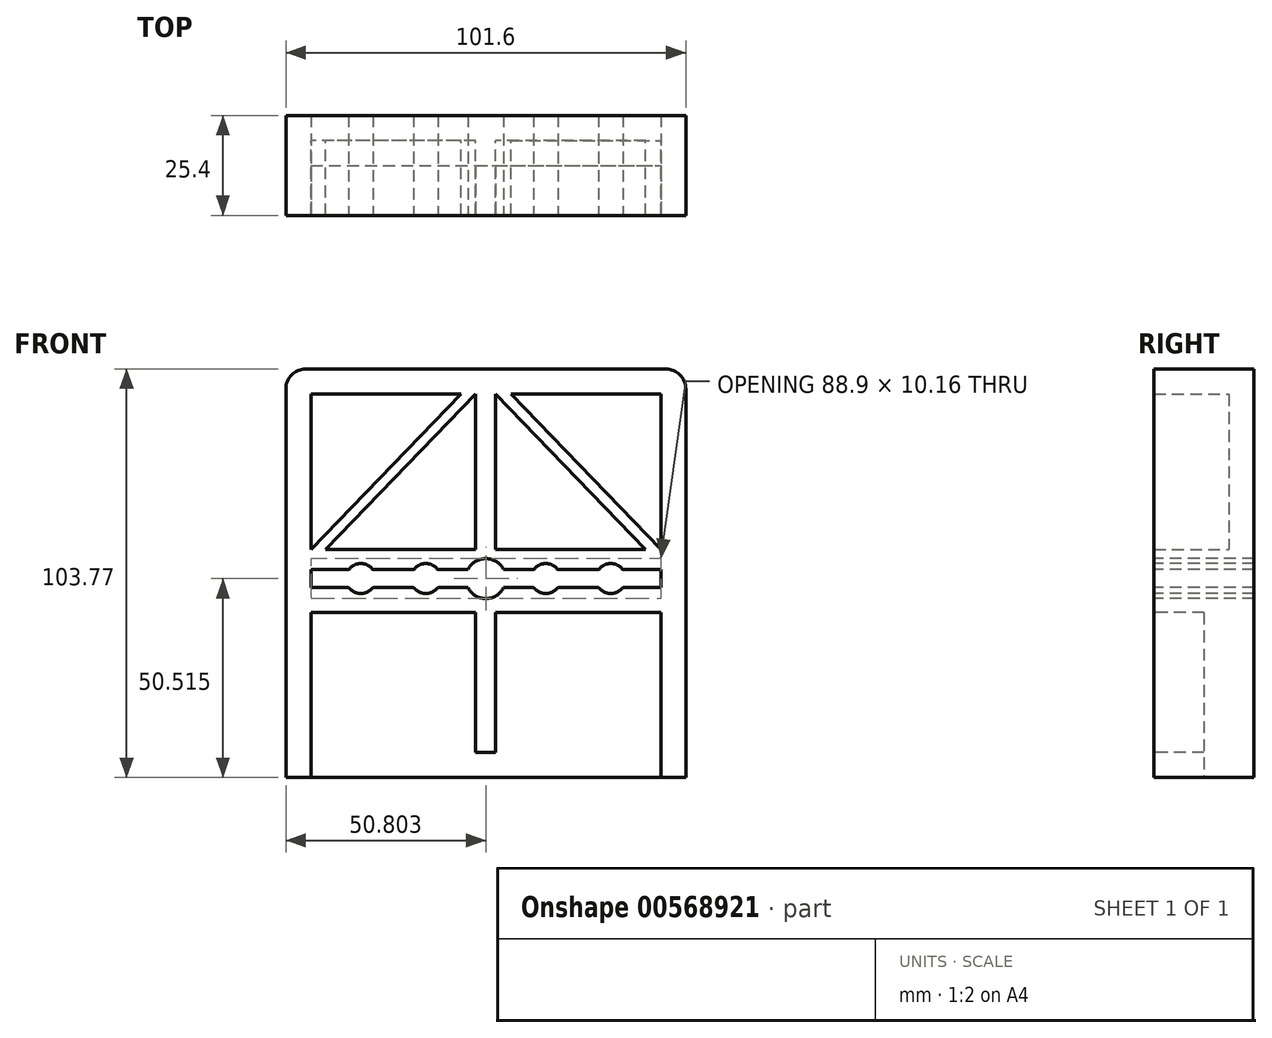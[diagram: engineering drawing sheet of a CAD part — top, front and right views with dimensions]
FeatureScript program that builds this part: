
annotation { "Feature Type Name" : "Feature", "Feature Type Description" : "" }
export const myFeature = defineFeature(function(context is Context, id is Id, definition is map)
    precondition{}
    {
        {
            var Q0;
            Q0=qCreatedBy(makeId("Front.planeOp"),FACE);
            var sketch = newSketch(context, id + "F0", { "sketchPlane" : qUnion([Q0])});
            skLineSegment(sketch, "E0.bottom", {"start": v(-51.37, 49.18) * mm, "end": v(50.23, 49.18) * mm});
            skLineSegment(sketch, "E0.top", {"start": v(-51.37, -54.59) * mm, "end": v(50.23, -54.59) * mm});
            skLineSegment(sketch, "E0.left", {"start": v(-51.37, 49.18) * mm, "end": v(-51.37, -54.59) * mm});
            skLineSegment(sketch, "E0.right", {"start": v(50.23, 49.18) * mm, "end": v(50.23, -54.59) * mm});
            skLineSegment(sketch, "E1", {"start": v(-45.02, 42.83) * mm, "end": v(-45.02, 3.28) * mm});
            skLineSegment(sketch, "E2", {"start": v(-45.02, 3.28) * mm, "end": v(-6.92, 42.83) * mm});
            skLineSegment(sketch, "E3", {"start": v(-6.92, 42.83) * mm, "end": v(-45.02, 42.83) * mm});
            skLineSegment(sketch, "E4", {"start": v(-41.2, 3.28) * mm, "end": v(-3.1, 42.83) * mm});
            skLineSegment(sketch, "E5", {"start": v(-3.1, 42.83) * mm, "end": v(-3.1, 3.28) * mm});
            skLineSegment(sketch, "E6", {"start": v(-3.1, 3.28) * mm, "end": v(-41.2, 3.28) * mm});
            skLineSegment(sketch, "E7", {"start": v(43.88, 42.83) * mm, "end": v(43.88, 3.28) * mm});
            skLineSegment(sketch, "E8", {"start": v(43.88, 3.28) * mm, "end": v(5.78, 42.83) * mm});
            skLineSegment(sketch, "E9", {"start": v(5.78, 42.83) * mm, "end": v(43.88, 42.83) * mm});
            skLineSegment(sketch, "E10", {"start": v(40.07, 3.28) * mm, "end": v(1.97, 42.83) * mm});
            skLineSegment(sketch, "E11", {"start": v(1.97, 42.83) * mm, "end": v(1.97, 3.28) * mm});
            skLineSegment(sketch, "E12", {"start": v(1.97, 3.28) * mm, "end": v(40.07, 3.28) * mm});
            skSolve(sketch);
        }
        {
            var Q0;
            Q0 = qSketchRegion(id + "F0", true);
            extrude(context, id + "F1", {"entities" : qUnion([Q0]), "depth" : 25.4 * mm, "offsetDistance" : 25.4 * mm});
        }
        {
            var Q0;
            Q0=makeQuery(id+"F0.imprint","IMPRINT",FACE,{"disambiguationData":[TD([[makeQuery(id+"F0.imprint","IMPRINT",EDGE,{"derivedFrom":sQuery(id+"F0.wireOp",EDGE,"E1")}),1.0]])]});
            var Q1;
            Q1=makeQuery(id+"F0.imprint","IMPRINT",FACE,{"disambiguationData":[TD([[makeQuery(id+"F0.imprint","IMPRINT",EDGE,{"derivedFrom":sQuery(id+"F0.wireOp",EDGE,"E4")}),-1.0]])]});
            var Q2;
            Q2=makeQuery(id+"F0.imprint","IMPRINT",FACE,{"disambiguationData":[TD([[makeQuery(id+"F0.imprint","IMPRINT",EDGE,{"derivedFrom":sQuery(id+"F0.wireOp",EDGE,"E10")}),1.0]])]});
            var Q3;
            Q3=makeQuery(id+"F0.imprint","IMPRINT",FACE,{"disambiguationData":[TD([[makeQuery(id+"F0.imprint","IMPRINT",EDGE,{"derivedFrom":sQuery(id+"F0.wireOp",EDGE,"E7")}),-1.0]])]});
            extrude(context, id + "F2", {"entities" : qUnion([Q0, Q1, Q2, Q3]), "operationType" : NewBodyOperationType.ADD, "depth" : 6.35 * mm, "offsetDistance" : 25.4 * mm});
        }
        {
            var Q0;
            Q0=makeQuery(id+"F1.opExtrude","SWEPT_EDGE",EDGE,{"disambiguationData":[OSD([sQuery(id+"F0.wireOp",EDGE,"E0.bottom"),sQuery(id+"F0.wireOp",EDGE,"E0.left")])]});
            var Q1;
            Q1=makeQuery(id+"F1.opExtrude","SWEPT_EDGE",EDGE,{"disambiguationData":[OSD([sQuery(id+"F0.wireOp",EDGE,"E0.bottom"),sQuery(id+"F0.wireOp",EDGE,"E0.right")])]});
            fillet(context, id + "F3", {"entities" : qUnion([Q0, Q1]), "radius" : 5.08 * mm, "tangentPropagation" : true, "allowEdgeOverflow" : false});
        }
        {
            var Q0;
            Q0=makeQuery(id+"F1.opExtrude","CAP_FACE",FACE,{"disambiguationData":[OSD([sQuery(id+"F0.wireOp",EDGE,"E0.bottom"),sQuery(id+"F0.wireOp",EDGE,"E0.top"),sQuery(id+"F0.wireOp",EDGE,"E0.left"),sQuery(id+"F0.wireOp",EDGE,"E0.right"),sQuery(id+"F0.wireOp",EDGE,"E1"),sQuery(id+"F0.wireOp",EDGE,"E2"),sQuery(id+"F0.wireOp",EDGE,"E3"),sQuery(id+"F0.wireOp",EDGE,"E4"),sQuery(id+"F0.wireOp",EDGE,"E5"),sQuery(id+"F0.wireOp",EDGE,"E6"),sQuery(id+"F0.wireOp",EDGE,"E7"),sQuery(id+"F0.wireOp",EDGE,"E8"),sQuery(id+"F0.wireOp",EDGE,"E9"),sQuery(id+"F0.wireOp",EDGE,"E10"),sQuery(id+"F0.wireOp",EDGE,"E11"),sQuery(id+"F0.wireOp",EDGE,"E12")])],"isStart":false});
            var sketch = newSketch(context, id + "F4", { "sketchPlane" : qUnion([Q0])});
            skLineSegment(sketch, "E13.bottom", {"start": v(-45.02, -1.8) * mm, "end": v(43.88, -1.8) * mm});
            skLineSegment(sketch, "E13.top", {"start": v(-45.02, -6.35) * mm, "end": v(43.88, -6.35) * mm});
            skLineSegment(sketch, "E13.left", {"start": v(-45.02, -1.8) * mm, "end": v(-45.02, -6.35) * mm});
            skLineSegment(sketch, "E13.right", {"start": v(43.88, -1.8) * mm, "end": v(43.88, -6.35) * mm});
            skSolve(sketch);
        }
        {
            var Q0;
            Q0=makeQuery(id+"F4.imprint","IMPRINT",FACE,{"disambiguationData":[TD([[makeQuery(id+"F4.imprint","IMPRINT",EDGE,{"derivedFrom":sQuery(id+"F4.wireOp",EDGE,"E13.bottom")}),-1.0]])]});
            extrude(context, id + "F5", {"entities" : qUnion([Q0]), "operationType" : NewBodyOperationType.REMOVE, "oppositeDirection" : true, "depth" : 25.4 * mm, "offsetDistance" : 25.4 * mm});
        }
        {
            var Q0;
            Q0=makeQuery(id+"F1.opExtrude","CAP_FACE",FACE,{"disambiguationData":[OSD([sQuery(id+"F0.wireOp",EDGE,"E0.bottom"),sQuery(id+"F0.wireOp",EDGE,"E0.top"),sQuery(id+"F0.wireOp",EDGE,"E0.left"),sQuery(id+"F0.wireOp",EDGE,"E0.right"),sQuery(id+"F0.wireOp",EDGE,"E1"),sQuery(id+"F0.wireOp",EDGE,"E2"),sQuery(id+"F0.wireOp",EDGE,"E3"),sQuery(id+"F0.wireOp",EDGE,"E4"),sQuery(id+"F0.wireOp",EDGE,"E5"),sQuery(id+"F0.wireOp",EDGE,"E6"),sQuery(id+"F0.wireOp",EDGE,"E7"),sQuery(id+"F0.wireOp",EDGE,"E8"),sQuery(id+"F0.wireOp",EDGE,"E9"),sQuery(id+"F0.wireOp",EDGE,"E10"),sQuery(id+"F0.wireOp",EDGE,"E11"),sQuery(id+"F0.wireOp",EDGE,"E12")])],"isStart":false});
            var sketch = newSketch(context, id + "F6", { "sketchPlane" : qUnion([Q0])});
            skLineSegment(sketch, "E14.bottom", {"start": v(-45.02, -12.7) * mm, "end": v(43.88, -12.7) * mm});
            skLineSegment(sketch, "E14.top", {"start": v(-45.02, -48.24) * mm, "end": v(43.88, -48.24) * mm});
            skLineSegment(sketch, "E14.left", {"start": v(-45.02, -12.7) * mm, "end": v(-45.02, -48.24) * mm});
            skLineSegment(sketch, "E14.right", {"start": v(43.88, -12.7) * mm, "end": v(43.88, -48.24) * mm});
            skLineSegment(sketch, "E15.bottom", {"start": v(-3.1, -12.7) * mm, "end": v(1.97, -12.7) * mm});
            skLineSegment(sketch, "E15.top", {"start": v(-3.1, -48.24) * mm, "end": v(1.97, -48.24) * mm});
            skLineSegment(sketch, "E15.left", {"start": v(-3.1, -12.7) * mm, "end": v(-3.1, -48.24) * mm});
            skLineSegment(sketch, "E15.right", {"start": v(1.97, -12.7) * mm, "end": v(1.97, -48.24) * mm});
            skSolve(sketch);
        }
        {
            var Q0;
            {var subQ0=sQuery(id+"F6.wireOp",EDGE,"E14.left");Q0=makeQuery(id+"F6.imprint","IMPRINT",FACE,{"disambiguationData":[TD([[makeQuery(id+"F6.imprint","IMPRINT",EDGE,{"derivedFrom":subQ0}),1.0]])]});}
            var Q1;
            {var subQ0=sQuery(id+"F6.wireOp",EDGE,"E14.right");Q1=makeQuery(id+"F6.imprint","IMPRINT",FACE,{"disambiguationData":[TD([[makeQuery(id+"F6.imprint","IMPRINT",EDGE,{"derivedFrom":subQ0}),-1.0]])]});}
            var Q2;
            Q2=makeQuery(id+"F6.imprint","IMPRINT",FACE,{"disambiguationData":[TD([[makeQuery(id+"F6.imprint","IMPRINT",EDGE,{"derivedFrom":sQuery(id+"F6.wireOp",EDGE,"E15.bottom")}),-1.0]])]});
            extrude(context, id + "F7", {"entities" : qUnion([Q0, Q1, Q2]), "operationType" : NewBodyOperationType.REMOVE, "oppositeDirection" : true, "depth" : 12.7 * mm, "offsetDistance" : 25.4 * mm});
        }
        {
            var Q0;
            Q0=makeQuery(id+"F1.opExtrude","CAP_FACE",FACE,{"disambiguationData":[OSD([sQuery(id+"F0.wireOp",EDGE,"E0.bottom"),sQuery(id+"F0.wireOp",EDGE,"E0.top"),sQuery(id+"F0.wireOp",EDGE,"E0.left"),sQuery(id+"F0.wireOp",EDGE,"E0.right"),sQuery(id+"F0.wireOp",EDGE,"E1"),sQuery(id+"F0.wireOp",EDGE,"E2"),sQuery(id+"F0.wireOp",EDGE,"E3"),sQuery(id+"F0.wireOp",EDGE,"E4"),sQuery(id+"F0.wireOp",EDGE,"E5"),sQuery(id+"F0.wireOp",EDGE,"E6"),sQuery(id+"F0.wireOp",EDGE,"E7"),sQuery(id+"F0.wireOp",EDGE,"E8"),sQuery(id+"F0.wireOp",EDGE,"E9"),sQuery(id+"F0.wireOp",EDGE,"E10"),sQuery(id+"F0.wireOp",EDGE,"E11"),sQuery(id+"F0.wireOp",EDGE,"E12")])],"isStart":false});
            var sketch = newSketch(context, id + "F8", { "sketchPlane" : qUnion([Q0])});
            skLineSegment(sketch, "E16.bottom", {"start": v(-45.02, -48.24) * mm, "end": v(43.88, -48.24) * mm});
            skLineSegment(sketch, "E16.top", {"start": v(-45.02, -54.59) * mm, "end": v(43.88, -54.59) * mm});
            skLineSegment(sketch, "E16.left", {"start": v(-45.02, -48.24) * mm, "end": v(-45.02, -54.59) * mm});
            skLineSegment(sketch, "E16.right", {"start": v(43.88, -48.24) * mm, "end": v(43.88, -54.59) * mm});
            skSolve(sketch);
        }
        {
            var Q0;
            Q0 = qSketchRegion(id + "F8", true);
            extrude(context, id + "F9", {"entities" : qUnion([Q0]), "operationType" : NewBodyOperationType.REMOVE, "oppositeDirection" : true, "depth" : 12.7 * mm, "offsetDistance" : 25.4 * mm});
        }
        {
            var Q0;
            Q0=makeQuery(id+"F1.opExtrude","CAP_FACE",FACE,{"disambiguationData":[OSD([sQuery(id+"F0.wireOp",EDGE,"E0.bottom"),sQuery(id+"F0.wireOp",EDGE,"E0.top"),sQuery(id+"F0.wireOp",EDGE,"E0.left"),sQuery(id+"F0.wireOp",EDGE,"E0.right"),sQuery(id+"F0.wireOp",EDGE,"E1"),sQuery(id+"F0.wireOp",EDGE,"E2"),sQuery(id+"F0.wireOp",EDGE,"E3"),sQuery(id+"F0.wireOp",EDGE,"E4"),sQuery(id+"F0.wireOp",EDGE,"E5"),sQuery(id+"F0.wireOp",EDGE,"E6"),sQuery(id+"F0.wireOp",EDGE,"E7"),sQuery(id+"F0.wireOp",EDGE,"E8"),sQuery(id+"F0.wireOp",EDGE,"E9"),sQuery(id+"F0.wireOp",EDGE,"E10"),sQuery(id+"F0.wireOp",EDGE,"E11"),sQuery(id+"F0.wireOp",EDGE,"E12")])],"isStart":false});
            var sketch = newSketch(context, id + "F10", { "sketchPlane" : qUnion([Q0])});
            skLineSegment(sketch, "E17", {"start": v(-45.02, -4.07) * mm, "end": v(43.88, -4.07) * mm});
            skCircle(sketch, "E18", {"center": v(-32.32, -4.07) * mm, "radius": 3.81 * mm});
            skCircle(sketch, "E19", {"center": v(31.18, -4.07) * mm, "radius": 3.81 * mm});
            skCircle(sketch, "E20", {"center": v(-15.8, -4.07) * mm, "radius": 3.81 * mm});
            skCircle(sketch, "E21", {"center": v(14.67, -4.07) * mm, "radius": 3.81 * mm});
            skCircle(sketch, "E22", {"center": v(-0.57, -4.07) * mm, "radius": 5.08 * mm});
            skSolve(sketch);
        }
        {
            var Q0;
            Q0 = qSketchRegion(id + "F10", true);
            extrude(context, id + "F11", {"entities" : qUnion([Q0]), "operationType" : NewBodyOperationType.REMOVE, "oppositeDirection" : true, "depth" : 25.4 * mm, "offsetDistance" : 25.4 * mm});
        }
    });
